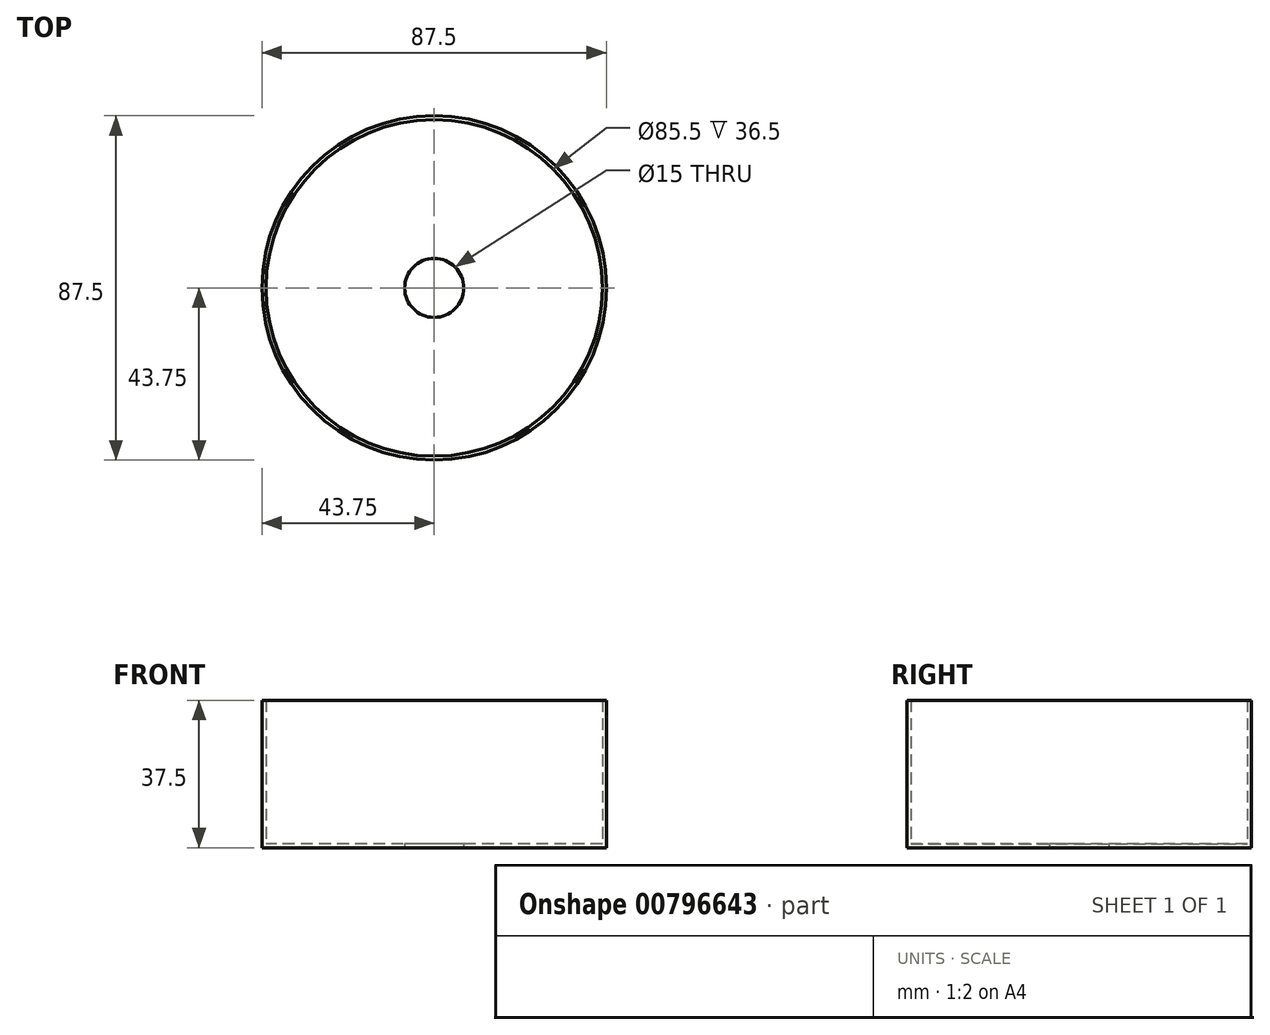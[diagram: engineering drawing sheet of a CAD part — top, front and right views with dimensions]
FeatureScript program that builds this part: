
annotation { "Feature Type Name" : "Feature", "Feature Type Description" : "" }
export const myFeature = defineFeature(function(context is Context, id is Id, definition is map)
    precondition{}
    {
        {
            var Q0;
            Q0=qCreatedBy(makeId("Top.planeOp"),FACE);
            var sketch = newSketch(context, id + "F0", { "sketchPlane" : qUnion([Q0])});
            skCircle(sketch, "E0", {"center": v(0, 0) * mm, "radius": 43.75 * mm});
            skSolve(sketch);
        }
        {
            var Q0;
            Q0 = qSketchRegion(id + "F0", true);
            extrude(context, id + "F1", {"entities" : qUnion([Q0]), "depth" : 37.5 * mm, "offsetDistance" : 25.4 * mm});
        }
        {
            var Q0;
            Q0=makeQuery(id+"F1.opExtrude","CAP_FACE",FACE,{"disambiguationData":[OSD([sQuery(id+"F0.wireOp",EDGE,"E0")])],"isStart":false});
            shell(context, id + "F2", {"entities" : qUnion([Q0]), "thickness" : 1 * mm});
        }
        {
            var Q0;
            Q0=makeQuery(id+"F1.opExtrude","CAP_FACE",FACE,{"disambiguationData":[OSD([sQuery(id+"F0.wireOp",EDGE,"E0")])],"isStart":true});
            var sketch = newSketch(context, id + "F3", { "sketchPlane" : qUnion([Q0])});
            skCircle(sketch, "E1", {"center": v(0, 0) * mm, "radius": 7.5 * mm});
            skSolve(sketch);
        }
        {
            var Q0;
            Q0=makeQuery(id+"F3.imprint","IMPRINT",FACE,{"disambiguationData":[TD([[makeQuery(id+"F3.imprint","IMPRINT",EDGE,{"derivedFrom":sQuery(id+"F3.wireOp",EDGE,"E1")}),1.0]])]});
            extrude(context, id + "F4", {"entities" : qUnion([Q0]), "operationType" : NewBodyOperationType.REMOVE, "oppositeDirection" : true, "depth" : 25.4 * mm, "offsetDistance" : 25.4 * mm});
        }
    });
